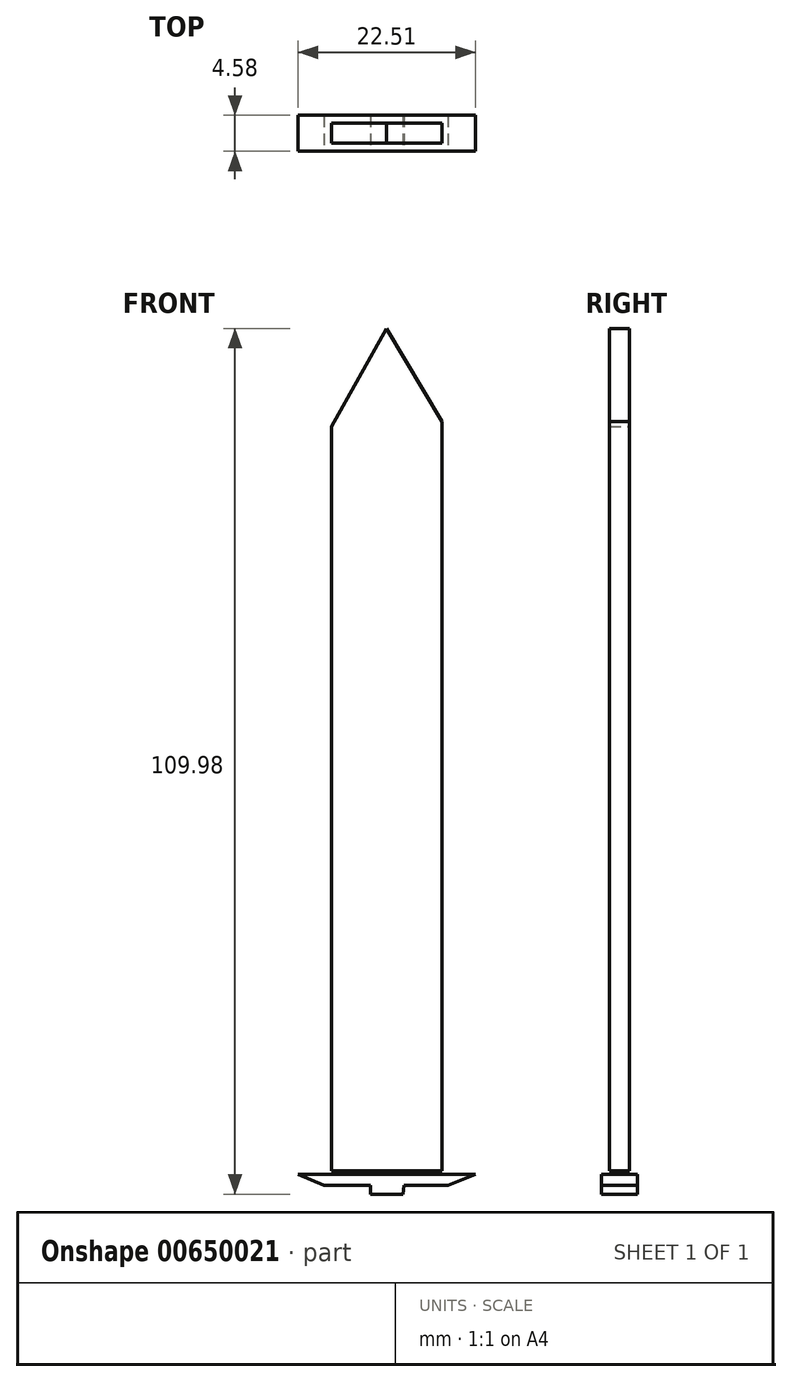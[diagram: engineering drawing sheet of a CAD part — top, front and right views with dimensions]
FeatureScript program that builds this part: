
annotation { "Feature Type Name" : "Feature", "Feature Type Description" : "" }
export const myFeature = defineFeature(function(context is Context, id is Id, definition is map)
    precondition{}
    {
        {
            var Q0;
            Q0=qCreatedBy(makeId("Front.planeOp"),FACE);
            var sketch = newSketch(context, id + "F0", { "sketchPlane" : qUnion([Q0])});
            skArc(sketch, "E0", {"start": v(0, -68.23) * mm, "mid": v(-5.05, -72.18) * mm, "end": v(0, -76.13) * mm});
            skLineSegment(sketch, "E1", {"start": v(0, -68.23) * mm, "end": v(0, -76.13) * mm});
            skLineSegment(sketch, "E2", {"start": v(0, -52.87) * mm, "end": v(-1.98, -52.87) * mm});
            skLineSegment(sketch, "E3", {"start": v(-1.98, -52.87) * mm, "end": v(-1.98, -68.23) * mm});
            skLineSegment(sketch, "E4", {"start": v(-1.98, -68.23) * mm, "end": v(0, -68.23) * mm});
            skLineSegment(sketch, "E5", {"start": v(0, -52.87) * mm, "end": v(0, -68.23) * mm});
            skSolve(sketch);
        }
        {
            var Q0;
            Q0=qCreatedBy(makeId("Front.planeOp"),FACE);
            var sketch = newSketch(context, id + "F1", { "sketchPlane" : qUnion([Q0])});
            skLineSegment(sketch, "E6", {"start": v(-2.05, -52.8) * mm, "end": v(2.1, -52.8) * mm});
            skLineSegment(sketch, "E7", {"start": v(-2.05, -52.8) * mm, "end": v(-2.05, -51.66) * mm});
            skLineSegment(sketch, "E8", {"start": v(-2.05, -51.66) * mm, "end": v(-7.98, -51.66) * mm});
            skLineSegment(sketch, "E9", {"start": v(-7.98, -51.66) * mm, "end": v(-11.25, -50.24) * mm});
            skLineSegment(sketch, "E10", {"start": v(-11.25, -50.24) * mm, "end": v(0, -50.24) * mm});
            skLineSegment(sketch, "E11", {"start": v(0, -50.24) * mm, "end": v(11.26, -50.24) * mm});
            skLineSegment(sketch, "E12", {"start": v(11.26, -50.24) * mm, "end": v(7.78, -51.66) * mm});
            skLineSegment(sketch, "E13", {"start": v(7.78, -51.66) * mm, "end": v(2.17, -51.66) * mm});
            skLineSegment(sketch, "E14", {"start": v(2.17, -51.66) * mm, "end": v(2.1, -52.8) * mm});
            skSolve(sketch);
        }
        {
            var Q0;
            Q0 = qSketchRegion(id + "F1", true);
            extrude(context, id + "F2", {"entities" : qUnion([Q0]), "oppositeDirection" : true, "depth" : 2.3 * mm, "offsetDistance" : 25.4 * mm, "hasSecondDirection" : true, "secondDirectionOppositeDirection" : false, "secondDirectionDepth" : 2.3 * mm});
        }
        {
            var Q0;
            Q0=qCreatedBy(makeId("Front.planeOp"),FACE);
            var sketch = newSketch(context, id + "F3", { "sketchPlane" : qUnion([Q0])});
            skLineSegment(sketch, "E15", {"start": v(0, -49.85) * mm, "end": v(7.04, -49.85) * mm});
            skLineSegment(sketch, "E16", {"start": v(7.04, -49.85) * mm, "end": v(0, -49.85) * mm});
            skLineSegment(sketch, "E17", {"start": v(0, -49.85) * mm, "end": v(-7.04, -49.85) * mm});
            skLineSegment(sketch, "E18", {"start": v(7.04, -49.85) * mm, "end": v(7.04, 45.36) * mm});
            skLineSegment(sketch, "E19", {"start": v(-7.04, -49.85) * mm, "end": v(-7.04, 44.7) * mm});
            skLineSegment(sketch, "E20", {"start": v(-7.04, 44.7) * mm, "end": v(0, 57.19) * mm});
            skLineSegment(sketch, "E21", {"start": v(0, 57.19) * mm, "end": v(7.04, 45.36) * mm});
            skSolve(sketch);
        }
        {
            var Q0;
            Q0 = qSketchRegion(id + "F3", true);
            extrude(context, id + "F4", {"entities" : qUnion([Q0]), "depth" : 1.27 * mm, "offsetDistance" : 25.4 * mm, "hasSecondDirection" : true, "secondDirectionOppositeDirection" : true, "secondDirectionDepth" : 1.27 * mm});
        }
    });
